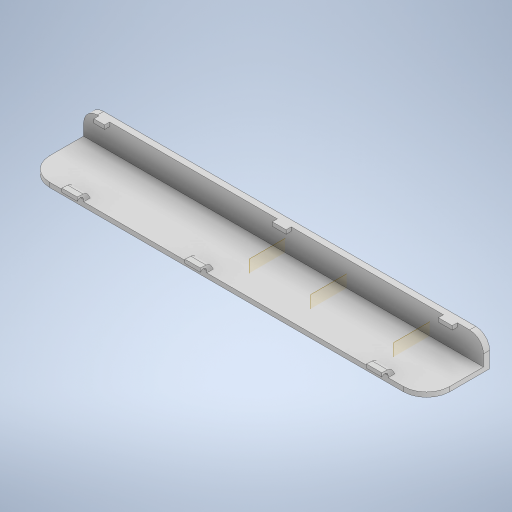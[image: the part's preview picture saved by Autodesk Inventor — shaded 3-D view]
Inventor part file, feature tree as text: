
AUTODESK INVENTOR PART (.ipt)
format: ipt  version: 2024.2 (Build 282272000, 272)  size: 327,168 bytes
history: native  units: mm
features: other x4, extrude x4, sketch x4, fillet x2, mirror x2
ambient origin geometry x8: Origin, YZ Plane, XZ Plane, XY Plane, X Axis, Y Axis, Z Axis, Center Point
bodies: Body1 (feature_tree)
feature tree (16):
  other  "Твердое тело1"
  extrude  "Выдавливание1"  Depth=20.5mm
  extrude  "Выдавливание2"  Depth=130.0mm
  fillet  "Сопряжение1"  Radius=7.5mm
  fillet  "Сопряжение2"  Radius=7.5mm
  extrude  "Выдавливание3"  Depth=1.5mm TaperAngle=0.0deg
  other  "РабПлоскость1"
  extrude  "Выдавливание4"  Depth=2.0mm
  other  "РабПлоскость2"
  mirror  "Зеркальное отражение1"
  other  "РабПлоскость3"
  mirror  "Зеркальное отражение2"
  sketch  "Эскиз1"
  sketch  "Эскиз2"
  sketch  "Эскиз3"
  sketch  "Эскиз4"
